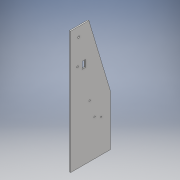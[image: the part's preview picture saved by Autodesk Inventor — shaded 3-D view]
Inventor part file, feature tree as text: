
AUTODESK INVENTOR PART (.ipt)
format: ipt  version: 2018 (Build 220112000, 112)  size: 124,416 bytes
history: native  units: mm
features: other x1, extrude x1, sketch x1
ambient origin geometry x8: Origin, YZ Plane, XZ Plane, XY Plane, X Axis, Y Axis, Z Axis, Center Point
bodies: Body1 (feature_tree)
feature tree (3):
  other  "ソリッド1"
  extrude  "押し出し1"  Depth=537.0mm
  sketch  "スケッチ1"
